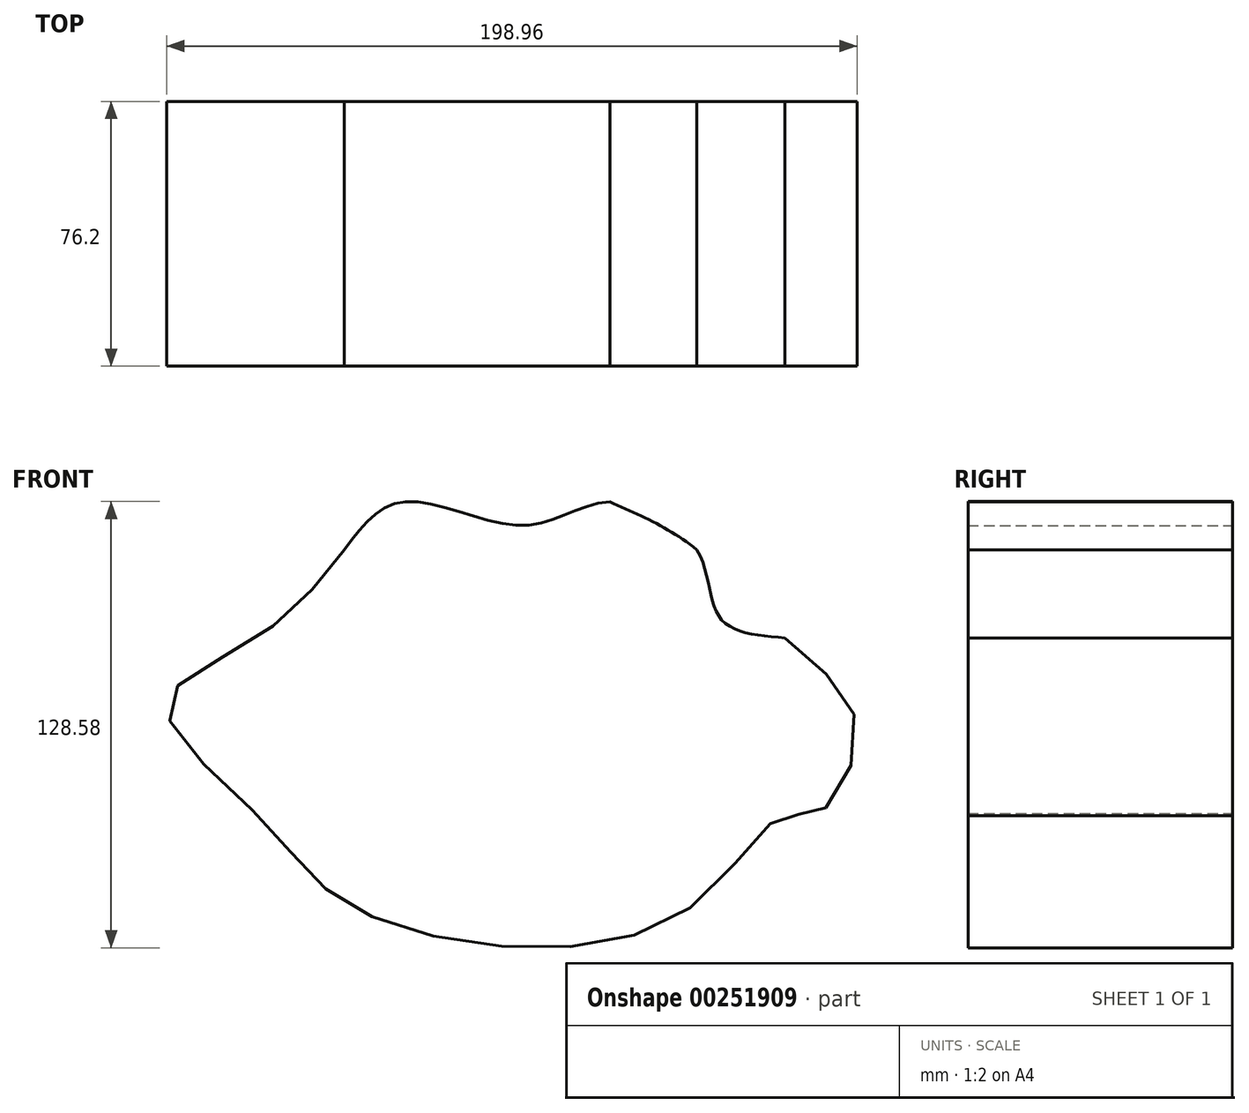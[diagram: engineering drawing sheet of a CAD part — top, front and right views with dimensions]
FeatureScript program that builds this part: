
annotation { "Feature Type Name" : "Feature", "Feature Type Description" : "" }
export const myFeature = defineFeature(function(context is Context, id is Id, definition is map)
    precondition{}
    {
        {
            var Q0;
            Q0=qCreatedBy(makeId("Front.planeOp"),FACE);
            var sketch = newSketch(context, id + "F0", { "sketchPlane" : qUnion([Q0])});
            skPoint(sketch, "E0.visualSharp", {"position": v(-76.96, 33.16) * mm});
            skPoint(sketch, "E1.visualSharp", {"position": v(75.44, 33.16) * mm});
            skPoint(sketch, "E2.visualSharp", {"position": v(75.44, -68.44) * mm});
            skPoint(sketch, "E3.visualSharp", {"position": v(-76.96, -68.44) * mm});
            skFitSpline(sketch, "E4", {"points": [v(-51.56, 33.16) * mm, v(-76.96, 7.76) * mm, v(-102.74, -11.62) * mm, v(-76.96, -43.04) * mm, v(-51.56, -68.44) * mm, v(0, -81.43) * mm, v(50.04, -68.44) * mm, v(75.44, -43.04) * mm, v(84.5, -43.04) * mm, v(96.08, -17.75) * mm, v(75.44, 7.76) * mm, v(50.04, 33.16) * mm, v(24.9, 46.96) * mm], "startDerivative": vector(-248.11, -319.61) * mm, "endDerivative": vector(-340.64, 148.62) * mm});
            skFitSpline(sketch, "E5", {"points": [v(75.44, 7.76) * mm, v(56.92, 13.24) * mm, v(50.04, 33.16) * mm, v(24.9, 46.96) * mm, v(0, 40.15) * mm, v(-34.35, 46.96) * mm, v(-51.56, 33.16) * mm], "startDerivative": vector(-154.18, 12.4) * mm, "endDerivative": vector(-92.24, -124.68) * mm});
            skSolve(sketch);
        }
        {
            var Q0;
            Q0=makeQuery(id+"F0.imprint","IMPRINT",FACE,{"disambiguationData":[TD([[makeQuery(id+"F0.imprint","IMPRINT",EDGE,{"derivedFrom":sQuery(id+"F0.wireOp",EDGE,"E4")}),1.0]])]});
            extrude(context, id + "F1", {"entities" : qUnion([Q0]), "depth" : 76.2 * mm});
        }
    });
